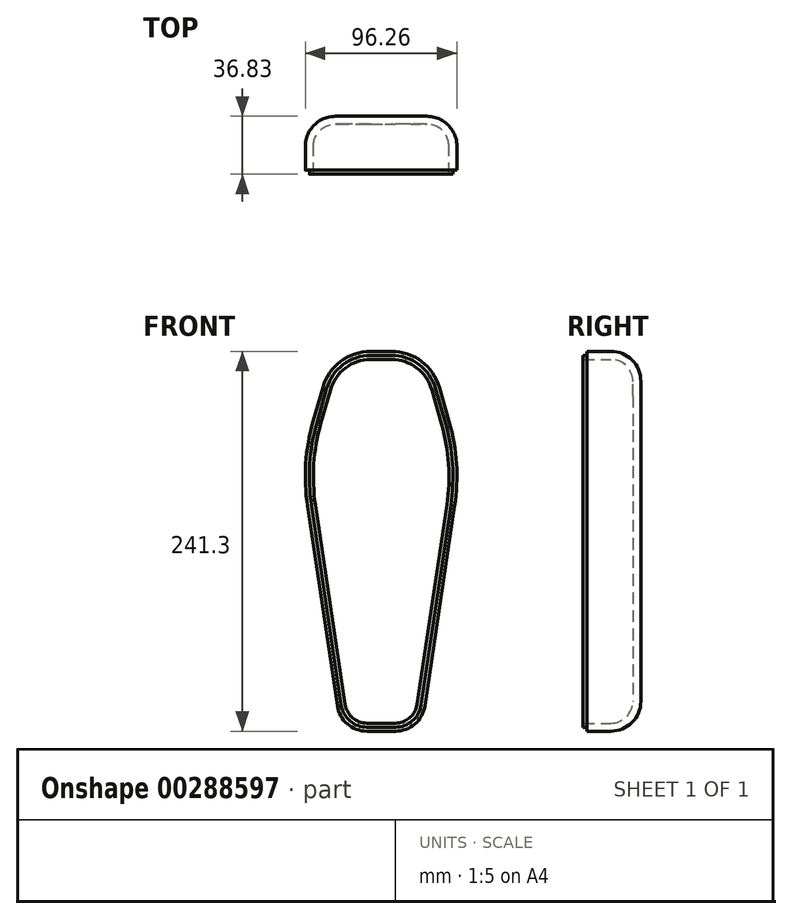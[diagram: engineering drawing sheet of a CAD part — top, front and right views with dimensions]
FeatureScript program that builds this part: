
annotation { "Feature Type Name" : "Feature", "Feature Type Description" : "" }
export const myFeature = defineFeature(function(context is Context, id is Id, definition is map)
    precondition{}
    {
        {
            var Q0;
            Q0=qCreatedBy(makeId("Front.planeOp"),FACE);
            var sketch = newSketch(context, id + "F0", { "sketchPlane" : qUnion([Q0])});
            skLineSegment(sketch, "E0", {"start": v(0, 48.06) * mm, "end": v(0, -193.24) * mm});
            skLineSegment(sketch, "E1", {"start": v(-30.48, 48.06) * mm, "end": v(0, 48.06) * mm});
            skPoint(sketch, "E2.visualSharp", {"position": v(-30.48, 48.06) * mm});
            skPoint(sketch, "E3.visualSharp", {"position": v(-25.4, -193.24) * mm});
            skLineSegment(sketch, "E4", {"start": v(-30.48, 48.06) * mm, "end": v(-50.8, -23.06) * mm});
            skLineSegment(sketch, "E5", {"start": v(-50.8, -23.06) * mm, "end": v(-25.4, -193.24) * mm});
            skLineSegment(sketch, "E6", {"start": v(-25.4, -193.24) * mm, "end": v(0, -193.24) * mm});
            skSolve(sketch);
        }
        {
            var Q0;
            Q0=qSketchRegion(id+"F0",true);
            extrude(context, id + "F1", {"entities" : qUnion([Q0]), "depth" : 34.3 * mm});
        }
        {
            var Q0;
            Q0=makeQuery(id+"F1.opExtrude","SWEPT_BODY",BODY,{"disambiguationData":[OSD([sQuery(id+"F0.wireOp",EDGE,"E0"),sQuery(id+"F0.wireOp",EDGE,"E1"),sQuery(id+"F0.wireOp",EDGE,"E4"),sQuery(id+"F0.wireOp",EDGE,"E5"),sQuery(id+"F0.wireOp",EDGE,"E6")])]});
            var Q1;
            Q1=makeQuery(id+"F1.opExtrude","SWEPT_FACE",FACE,{"disambiguationData":[OSD([sQuery(id+"F0.wireOp",EDGE,"E0")])]});
            mirror(context, id + "F2", {"operationType" : NewBodyOperationType.ADD, "entities" : qUnion([Q0]), "mirrorPlane" : qUnion([Q1])});
        }
        {
            var Q0;
            Q0=makeQuery(id+"F1.opExtrude","SWEPT_EDGE",EDGE,{"disambiguationData":[OSD([sQuery(id+"F0.wireOp",EDGE,"E1"),sQuery(id+"F0.wireOp",EDGE,"E4")])]});
            var Q1;
            Q1=makeQuery(id+"F2.opPattern","COPY",EDGE,{"derivedFrom":makeQuery(id+"F1.opExtrude","SWEPT_EDGE",EDGE,{"disambiguationData":[OSD([sQuery(id+"F0.wireOp",EDGE,"E1"),sQuery(id+"F0.wireOp",EDGE,"E4")])]}),"instanceName":"1"});
            fillet(context, id + "F3", {"entities" : qUnion([Q0, Q1]), "radius" : 31.75 * mm, "tangentPropagation" : true, "allowEdgeOverflow" : false});
        }
        {
            var Q0;
            Q0=makeQuery(id+"F1.opExtrude","SWEPT_EDGE",EDGE,{"disambiguationData":[OSD([sQuery(id+"F0.wireOp",EDGE,"E4"),sQuery(id+"F0.wireOp",EDGE,"E5")])]});
            var Q1;
            Q1=makeQuery(id+"F2.opPattern","COPY",EDGE,{"derivedFrom":makeQuery(id+"F1.opExtrude","SWEPT_EDGE",EDGE,{"disambiguationData":[OSD([sQuery(id+"F0.wireOp",EDGE,"E4"),sQuery(id+"F0.wireOp",EDGE,"E5")])]}),"instanceName":"1"});
            fillet(context, id + "F4", {"entities" : qUnion([Q0, Q1]), "radius" : 127 * mm, "tangentPropagation" : true, "allowEdgeOverflow" : false});
        }
        {
            var Q0;
            Q0=makeQuery(id+"F1.opExtrude","SWEPT_EDGE",EDGE,{"disambiguationData":[OSD([sQuery(id+"F0.wireOp",EDGE,"E5"),sQuery(id+"F0.wireOp",EDGE,"E6")])]});
            var Q1;
            Q1=makeQuery(id+"F2.opPattern","COPY",EDGE,{"derivedFrom":makeQuery(id+"F1.opExtrude","SWEPT_EDGE",EDGE,{"disambiguationData":[OSD([sQuery(id+"F0.wireOp",EDGE,"E5"),sQuery(id+"F0.wireOp",EDGE,"E6")])]}),"instanceName":"1"});
            fillet(context, id + "F5", {"entities" : qUnion([Q0, Q1]), "radius" : 19.05 * mm, "tangentPropagation" : true, "allowEdgeOverflow" : false});
        }
        {
            var Q0;
            Q0=makeQuery(id+"F2.opPattern","COPY",EDGE,{"derivedFrom":makeQuery(id+"F1.opExtrude","CAP_EDGE",EDGE,{"disambiguationData":[OSD([sQuery(id+"F0.wireOp",EDGE,"E5")])],"isStart":true}),"instanceName":"1"});
            fillet(context, id + "F6", {"entities" : qUnion([Q0]), "radius" : 19.05 * mm, "tangentPropagation" : true, "allowEdgeOverflow" : false});
        }
        {
            var Q0;
            {var subQ0=makeQuery(id+"F1.opExtrude","CAP_FACE",FACE,{"disambiguationData":[OSD([sQuery(id+"F0.wireOp",EDGE,"E0"),sQuery(id+"F0.wireOp",EDGE,"E1"),sQuery(id+"F0.wireOp",EDGE,"E4"),sQuery(id+"F0.wireOp",EDGE,"E5"),sQuery(id+"F0.wireOp",EDGE,"E6")])],"isStart":false});Q0=makeQuery(id+"F2.boolean.opBoolean","MERGE",FACE,{"derivedFrom":[subQ0,makeQuery(id+"F2.opPattern","COPY",FACE,{"derivedFrom":subQ0,"instanceName":"1"})]});}
            shell(context, id + "F7", {"entities" : qUnion([Q0]), "thickness" : 5.08 * mm});
        }
        {
            var Q0;
            {var subQ0=makeQuery(id+"F1.opExtrude","CAP_FACE",FACE,{"disambiguationData":[OSD([sQuery(id+"F0.wireOp",EDGE,"E0"),sQuery(id+"F0.wireOp",EDGE,"E1"),sQuery(id+"F0.wireOp",EDGE,"E4"),sQuery(id+"F0.wireOp",EDGE,"E5"),sQuery(id+"F0.wireOp",EDGE,"E6")])],"isStart":false});Q0=makeQuery(id+"F2.boolean.opBoolean","MERGE",FACE,{"derivedFrom":[subQ0,makeQuery(id+"F2.opPattern","COPY",FACE,{"derivedFrom":subQ0,"instanceName":"1"})]});}
            var sketch = newSketch(context, id + "F8", { "sketchPlane" : qUnion([Q0])});
            skLineSegment(sketch, "E7.0", {"start": v(-6.53, 45.52) * mm, "end": v(6.53, 45.52) * mm});
            skArc(sketch, "E7.1", {"start": v(-25.31, -176.62) * mm, "mid": v(-19.76, -186.7) * mm, "end": v(-8.98, -190.7) * mm});
            skLineSegment(sketch, "E7.2", {"start": v(-44.23, -49.88) * mm, "end": v(-25.31, -176.62) * mm});
            skArc(sketch, "E7.3", {"start": v(-40.8, 2.69) * mm, "mid": v(-45.33, -23.41) * mm, "end": v(-44.23, -49.88) * mm});
            skLineSegment(sketch, "E7.4", {"start": v(-34.62, 24.34) * mm, "end": v(-40.8, 2.69) * mm});
            skLineSegment(sketch, "E7.5", {"start": v(-8.98, -190.7) * mm, "end": v(8.98, -190.7) * mm});
            skArc(sketch, "E7.6", {"start": v(-6.53, 45.52) * mm, "mid": v(-24.12, 39.63) * mm, "end": v(-34.62, 24.34) * mm});
            skArc(sketch, "E7.7", {"start": v(8.98, -190.7) * mm, "mid": v(19.76, -186.7) * mm, "end": v(25.31, -176.62) * mm});
            skLineSegment(sketch, "E7.8", {"start": v(44.23, -49.88) * mm, "end": v(25.31, -176.62) * mm});
            skArc(sketch, "E7.9", {"start": v(44.23, -49.88) * mm, "mid": v(45.33, -23.41) * mm, "end": v(40.8, 2.69) * mm});
            skLineSegment(sketch, "E7.10", {"start": v(34.62, 24.34) * mm, "end": v(40.8, 2.69) * mm});
            skArc(sketch, "E7.11", {"start": v(34.62, 24.34) * mm, "mid": v(24.12, 39.63) * mm, "end": v(6.53, 45.52) * mm});
            skLineSegment(sketch, "E8.0", {"start": v(-6.53, 42.98) * mm, "end": v(6.53, 42.98) * mm});
            skArc(sketch, "E8.1", {"start": v(32.17, 23.64) * mm, "mid": v(22.6, 37.6) * mm, "end": v(6.53, 42.98) * mm});
            skLineSegment(sketch, "E8.2", {"start": v(32.17, 23.64) * mm, "end": v(38.36, 1.99) * mm});
            skArc(sketch, "E8.3", {"start": v(41.72, -49.5) * mm, "mid": v(42.8, -23.58) * mm, "end": v(38.36, 1.99) * mm});
            skLineSegment(sketch, "E8.4", {"start": v(41.72, -49.5) * mm, "end": v(22.8, -176.25) * mm});
            skArc(sketch, "E8.5", {"start": v(8.98, -188.16) * mm, "mid": v(18.1, -184.77) * mm, "end": v(22.8, -176.25) * mm});
            skLineSegment(sketch, "E8.6", {"start": v(-8.98, -188.16) * mm, "end": v(8.98, -188.16) * mm});
            skArc(sketch, "E8.7", {"start": v(-22.8, -176.25) * mm, "mid": v(-18.1, -184.77) * mm, "end": v(-8.98, -188.16) * mm});
            skLineSegment(sketch, "E8.8", {"start": v(-41.72, -49.5) * mm, "end": v(-22.8, -176.25) * mm});
            skArc(sketch, "E8.9", {"start": v(-38.36, 1.99) * mm, "mid": v(-42.8, -23.58) * mm, "end": v(-41.72, -49.5) * mm});
            skLineSegment(sketch, "E8.10", {"start": v(-32.17, 23.64) * mm, "end": v(-38.36, 1.99) * mm});
            skArc(sketch, "E8.11", {"start": v(-6.53, 42.98) * mm, "mid": v(-22.6, 37.6) * mm, "end": v(-32.17, 23.64) * mm});
            skSolve(sketch);
        }
        {
            var Q0;
            Q0=qSketchRegion(id+"F8",true);
            extrude(context, id + "F9", {"entities" : qUnion([Q0]), "operationType" : NewBodyOperationType.ADD, "depth" : 2.54 * mm});
        }
    });
